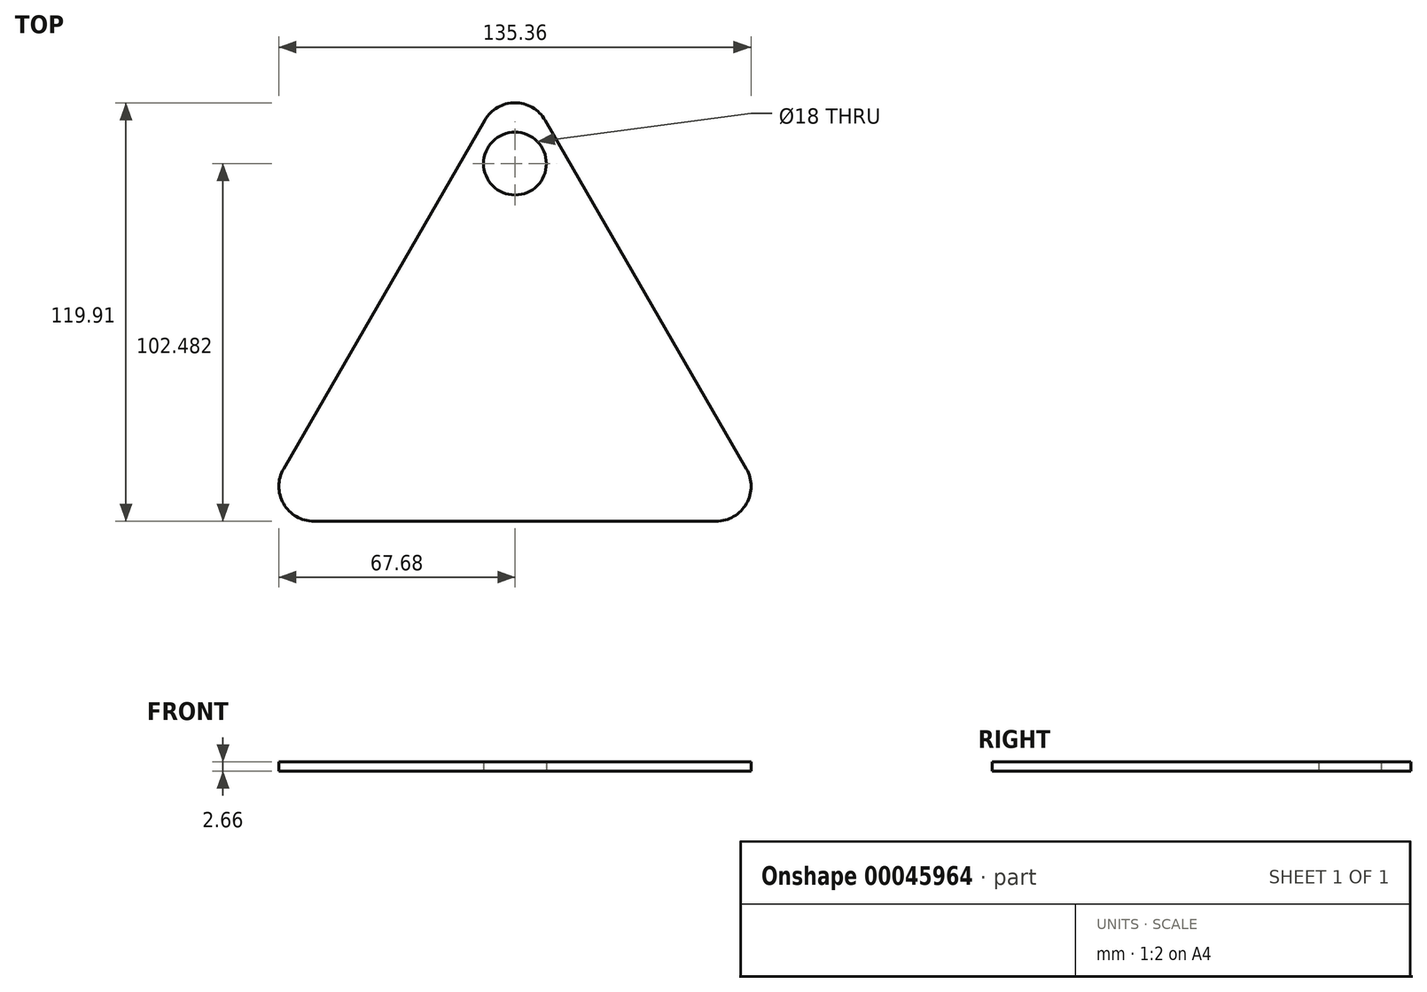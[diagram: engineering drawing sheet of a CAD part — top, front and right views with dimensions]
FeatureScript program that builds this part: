
annotation { "Feature Type Name" : "Feature", "Feature Type Description" : "" }
export const myFeature = defineFeature(function(context is Context, id is Id, definition is map)
    precondition{}
    {
        {
            var Q0;
            Q0=qCreatedBy(makeId("Top.planeOp"),FACE);
            var sketch = newSketch(context, id + "F0", { "sketchPlane" : qUnion([Q0])});
            skCircle(sketch, "E0.cCircle", {"center": v(0, -13.1) * mm, "radius": 86.6 * mm, "construction": true});
            skLineSegment(sketch, "E0.0", {"start": v(57.68, -56.4) * mm, "end": v(-57.68, -56.4) * mm});
            skLineSegment(sketch, "E0.1", {"start": v(-66.34, -41.4) * mm, "end": v(-8.66, 58.5) * mm});
            skLineSegment(sketch, "E0.2", {"start": v(8.66, 58.5) * mm, "end": v(66.34, -41.4) * mm});
            skPoint(sketch, "E1.visualSharp", {"position": v(0, 73.5) * mm});
            skArc(sketch, "E1.filletArc", {"start": v(8.66, 58.5) * mm, "mid": v(0, 63.5) * mm, "end": v(-8.66, 58.5) * mm});
            skPoint(sketch, "E2.visualSharp", {"position": v(75, -56.4) * mm});
            skArc(sketch, "E2.filletArc", {"start": v(57.68, -56.4) * mm, "mid": v(66.34, -51.4) * mm, "end": v(66.34, -41.4) * mm});
            skPoint(sketch, "E3.visualSharp", {"position": v(-75, -56.4) * mm});
            skArc(sketch, "E3.filletArc", {"start": v(-66.34, -41.4) * mm, "mid": v(-66.34, -51.4) * mm, "end": v(-57.68, -56.4) * mm});
            skCircle(sketch, "E4", {"center": v(0, 46.07) * mm, "radius": 9 * mm});
            skSolve(sketch);
        }
        {
            var Q0;
            Q0 = qSketchRegion(id + "F0", true);
            extrude(context, id + "F1", {"entities" : qUnion([Q0]), "depth" : 2.66 * mm});
        }
    });
